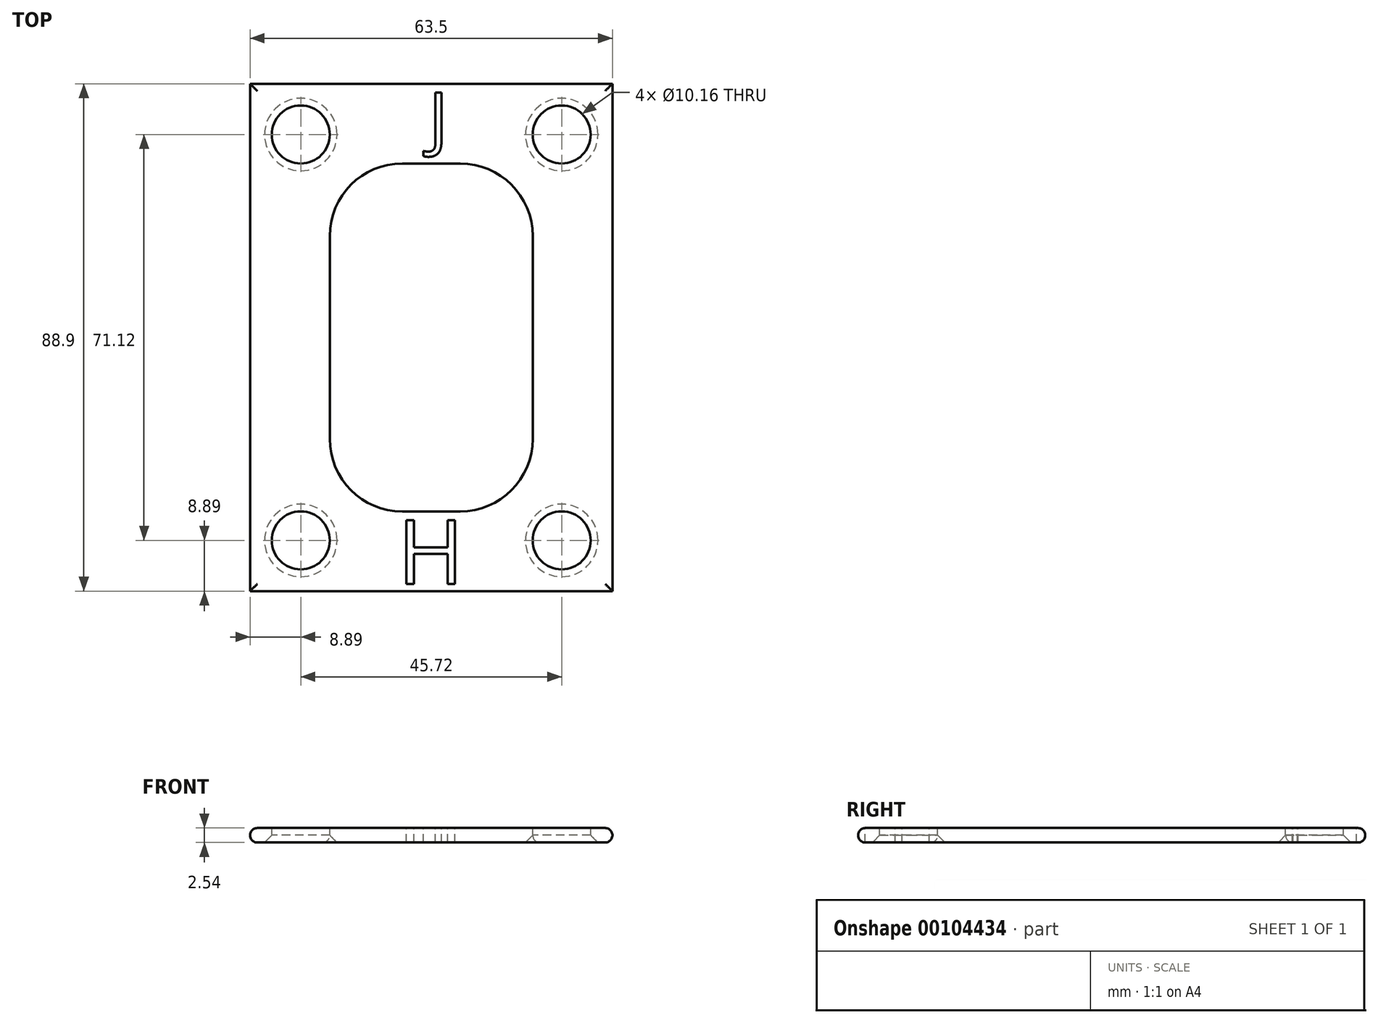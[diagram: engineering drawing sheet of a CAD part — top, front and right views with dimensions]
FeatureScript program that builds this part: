
annotation { "Feature Type Name" : "Feature", "Feature Type Description" : "" }
export const myFeature = defineFeature(function(context is Context, id is Id, definition is map)
    precondition{}
    {
        {
            var Q0;
            Q0=qCreatedBy(makeId("Top.planeOp"),FACE);
            var sketch = newSketch(context, id + "F0", { "sketchPlane" : qUnion([Q0])});
            skPoint(sketch, "E0", {"position": v(0, 88.9) * mm});
            skPoint(sketch, "E1", {"position": v(63.5, 0) * mm});
            skLineSegment(sketch, "E2.bottom", {"start": v(0, 88.9) * mm, "end": v(63.5, 88.9) * mm});
            skLineSegment(sketch, "E2.top", {"start": v(0, 0) * mm, "end": v(63.5, 0) * mm});
            skLineSegment(sketch, "E2.left", {"start": v(0, 88.9) * mm, "end": v(0, 0) * mm});
            skLineSegment(sketch, "E2.right", {"start": v(63.5, 88.9) * mm, "end": v(63.5, 0) * mm});
            skSolve(sketch);
        }
        {
            var Q0;
            Q0 = qSketchRegion(id + "F0", true);
            extrude(context, id + "F1", {"entities" : qUnion([Q0]), "depth" : 2.54 * mm});
        }
        {
            var Q0;
            Q0=makeQuery(id+"F1.opExtrude","CAP_EDGE",EDGE,{"disambiguationData":[OSD([sQuery(id+"F0.wireOp",EDGE,"E2.right")])],"isStart":false});
            var Q1;
            Q1=makeQuery(id+"F1.opExtrude","CAP_EDGE",EDGE,{"disambiguationData":[OSD([sQuery(id+"F0.wireOp",EDGE,"E2.top")])],"isStart":false});
            var Q2;
            Q2=makeQuery(id+"F1.opExtrude","CAP_EDGE",EDGE,{"disambiguationData":[OSD([sQuery(id+"F0.wireOp",EDGE,"E2.bottom")])],"isStart":false});
            var Q3;
            Q3=makeQuery(id+"F1.opExtrude","CAP_EDGE",EDGE,{"disambiguationData":[OSD([sQuery(id+"F0.wireOp",EDGE,"E2.left")])],"isStart":false});
            var Q4;
            Q4=makeQuery(id+"F1.opExtrude","CAP_FACE",FACE,{"disambiguationData":[OSD([sQuery(id+"F0.wireOp",EDGE,"E2.bottom"),sQuery(id+"F0.wireOp",EDGE,"E2.top"),sQuery(id+"F0.wireOp",EDGE,"E2.left"),sQuery(id+"F0.wireOp",EDGE,"E2.right")])],"isStart":true});
            var Q5;
            Q5=makeQuery(id+"F1.opExtrude","CAP_EDGE",EDGE,{"disambiguationData":[OSD([sQuery(id+"F0.wireOp",EDGE,"E2.left")])],"isStart":true});
            var Q6;
            Q6=makeQuery(id+"F1.opExtrude","CAP_EDGE",EDGE,{"disambiguationData":[OSD([sQuery(id+"F0.wireOp",EDGE,"E2.right")])],"isStart":true});
            var Q7;
            Q7=makeQuery(id+"F1.opExtrude","CAP_EDGE",EDGE,{"disambiguationData":[OSD([sQuery(id+"F0.wireOp",EDGE,"E2.bottom")])],"isStart":true});
            var Q8;
            Q8=makeQuery(id+"F1.opExtrude","CAP_EDGE",EDGE,{"disambiguationData":[OSD([sQuery(id+"F0.wireOp",EDGE,"E2.top")])],"isStart":true});
            fillet(context, id + "F2", {"entities" : qUnion([Q0, Q1, Q2, Q3, Q4, Q5, Q6, Q7, Q8]), "radius" : 1.27 * mm, "tangentPropagation" : true, "allowEdgeOverflow" : false});
        }
        {
            var Q0;
            Q0=makeQuery(id+"F1.opExtrude","CAP_FACE",FACE,{"disambiguationData":[OSD([sQuery(id+"F0.wireOp",EDGE,"E2.bottom"),sQuery(id+"F0.wireOp",EDGE,"E2.top"),sQuery(id+"F0.wireOp",EDGE,"E2.left"),sQuery(id+"F0.wireOp",EDGE,"E2.right")])],"isStart":false});
            var sketch = newSketch(context, id + "F3", { "sketchPlane" : qUnion([Q0])});
            skPoint(sketch, "E3", {"position": v(31.75, 44.45) * mm});
            skPoint(sketch, "E3.positionSnap0", {"position": v(1.27, 44.45) * mm});
            skPoint(sketch, "E3.positionSnap1", {"position": v(31.75, 87.63) * mm});
            skPoint(sketch, "E4", {"position": v(13.97, 74.93) * mm});
            skPoint(sketch, "E5", {"position": v(49.53, 74.93) * mm});
            skPoint(sketch, "E6", {"position": v(49.53, 13.97) * mm});
            skLineSegment(sketch, "E7.bottom", {"start": v(26.67, 74.93) * mm, "end": v(36.83, 74.93) * mm});
            skLineSegment(sketch, "E7.top", {"start": v(26.67, 13.97) * mm, "end": v(36.83, 13.97) * mm});
            skLineSegment(sketch, "E7.left", {"start": v(13.97, 62.23) * mm, "end": v(13.97, 26.67) * mm});
            skLineSegment(sketch, "E7.right", {"start": v(49.53, 62.23) * mm, "end": v(49.53, 26.67) * mm});
            skArc(sketch, "E8.filletArc", {"start": v(49.53, 62.23) * mm, "mid": v(45.81, 71.21) * mm, "end": v(36.83, 74.93) * mm});
            skArc(sketch, "E9.filletArc", {"start": v(26.67, 74.93) * mm, "mid": v(17.69, 71.21) * mm, "end": v(13.97, 62.23) * mm});
            skPoint(sketch, "E10.visualSharp", {"position": v(13.97, 13.97) * mm});
            skArc(sketch, "E10.filletArc", {"start": v(13.97, 26.67) * mm, "mid": v(17.69, 17.69) * mm, "end": v(26.67, 13.97) * mm});
            skArc(sketch, "E11.filletArc", {"start": v(36.83, 13.97) * mm, "mid": v(45.81, 17.69) * mm, "end": v(49.53, 26.67) * mm});
            skSolve(sketch);
        }
        {
            var Q0;
            Q0 = qSketchRegion(id + "F3", true);
            extrude(context, id + "F4", {"entities" : qUnion([Q0]), "operationType" : NewBodyOperationType.REMOVE, "endBound" : BoundingType.THROUGH_ALL, "oppositeDirection" : true, "depth" : 25.4 * mm});
        }
        {
            var Q0;
            Q0=makeQuery(id+"F4.boolean.opBoolean","COPY",EDGE,{"derivedFrom":makeQuery(id+"F4.opExtrude","CAP_EDGE",EDGE,{"disambiguationData":[OSD([sQuery(id+"F3.wireOp",EDGE,"E8.filletArc")])],"isStart":true})});
            var Q1;
            Q1=makeQuery(id+"F4.boolean.opBoolean","INTERSECT",EDGE,{"derivedFrom":[makeQuery(id+"F1.opExtrude","CAP_FACE",FACE,{"disambiguationData":[OSD([sQuery(id+"F0.wireOp",EDGE,"E2.bottom"),sQuery(id+"F0.wireOp",EDGE,"E2.top"),sQuery(id+"F0.wireOp",EDGE,"E2.left"),sQuery(id+"F0.wireOp",EDGE,"E2.right")])],"isStart":true}),makeQuery(id+"F4.opExtrude","SWEPT_FACE",FACE,{"disambiguationData":[OSD([sQuery(id+"F3.wireOp",EDGE,"E7.left")])]})]});
            fillet(context, id + "F5", {"entities" : qUnion([Q0, Q1]), "radius" : 1.27 * mm, "tangentPropagation" : true, "allowEdgeOverflow" : false});
        }
        {
            var Q0;
            Q0=makeQuery(id+"F1.opExtrude","CAP_FACE",FACE,{"disambiguationData":[OSD([sQuery(id+"F0.wireOp",EDGE,"E2.bottom"),sQuery(id+"F0.wireOp",EDGE,"E2.top"),sQuery(id+"F0.wireOp",EDGE,"E2.left"),sQuery(id+"F0.wireOp",EDGE,"E2.right")])],"isStart":false});
            var sketch = newSketch(context, id + "F6", { "sketchPlane" : qUnion([Q0])});
            skPoint(sketch, "E12", {"position": v(8.9, 80.01) * mm});
            skPoint(sketch, "E13", {"position": v(54.6, 80.01) * mm});
            skPoint(sketch, "E14", {"position": v(54.6, 8.9) * mm});
            skPoint(sketch, "E15", {"position": v(8.9, 8.9) * mm});
            skPoint(sketch, "E16", {"position": v(13.97, 80.01) * mm});
            skPoint(sketch, "E17", {"position": v(13.97, 8.9) * mm});
            skPoint(sketch, "E18", {"position": v(49.53, 80.01) * mm});
            skPoint(sketch, "E19", {"position": v(49.53, 8.9) * mm});
            skCircle(sketch, "E20", {"center": v(8.9, 80.01) * mm, "radius": 5.08 * mm});
            skCircle(sketch, "E21", {"center": v(54.6, 80.01) * mm, "radius": 5.08 * mm});
            skCircle(sketch, "E22", {"center": v(54.6, 8.9) * mm, "radius": 5.08 * mm});
            skCircle(sketch, "E23", {"center": v(8.9, 8.9) * mm, "radius": 5.08 * mm});
            skSolve(sketch);
        }
        {
            var Q0;
            Q0 = qSketchRegion(id + "F6", true);
            extrude(context, id + "F7", {"entities" : qUnion([Q0]), "operationType" : NewBodyOperationType.REMOVE, "endBound" : BoundingType.THROUGH_ALL, "oppositeDirection" : true, "depth" : 25.4 * mm});
        }
        {
            var Q0;
            Q0=makeQuery(id+"F7.boolean.opBoolean","INTERSECT",EDGE,{"derivedFrom":[makeQuery(id+"F1.opExtrude","CAP_FACE",FACE,{"disambiguationData":[OSD([sQuery(id+"F0.wireOp",EDGE,"E2.bottom"),sQuery(id+"F0.wireOp",EDGE,"E2.top"),sQuery(id+"F0.wireOp",EDGE,"E2.left"),sQuery(id+"F0.wireOp",EDGE,"E2.right")])],"isStart":true}),makeQuery(id+"F7.opExtrude","SWEPT_FACE",FACE,{"disambiguationData":[OSD([sQuery(id+"F6.wireOp",EDGE,"E20")])]})]});
            var Q1;
            Q1=makeQuery(id+"F7.boolean.opBoolean","COPY",EDGE,{"derivedFrom":makeQuery(id+"F7.opExtrude","CAP_EDGE",EDGE,{"disambiguationData":[OSD([sQuery(id+"F6.wireOp",EDGE,"E20")])],"isStart":true})});
            var Q2;
            Q2=makeQuery(id+"F7.boolean.opBoolean","COPY",EDGE,{"derivedFrom":makeQuery(id+"F7.opExtrude","CAP_EDGE",EDGE,{"disambiguationData":[OSD([sQuery(id+"F6.wireOp",EDGE,"E21")])],"isStart":true})});
            var Q3;
            Q3=makeQuery(id+"F7.boolean.opBoolean","INTERSECT",EDGE,{"derivedFrom":[makeQuery(id+"F1.opExtrude","CAP_FACE",FACE,{"disambiguationData":[OSD([sQuery(id+"F0.wireOp",EDGE,"E2.bottom"),sQuery(id+"F0.wireOp",EDGE,"E2.top"),sQuery(id+"F0.wireOp",EDGE,"E2.left"),sQuery(id+"F0.wireOp",EDGE,"E2.right")])],"isStart":true}),makeQuery(id+"F7.opExtrude","SWEPT_FACE",FACE,{"disambiguationData":[OSD([sQuery(id+"F6.wireOp",EDGE,"E21")])]})]});
            var Q4;
            Q4=makeQuery(id+"F7.boolean.opBoolean","INTERSECT",EDGE,{"derivedFrom":[makeQuery(id+"F1.opExtrude","CAP_FACE",FACE,{"disambiguationData":[OSD([sQuery(id+"F0.wireOp",EDGE,"E2.bottom"),sQuery(id+"F0.wireOp",EDGE,"E2.top"),sQuery(id+"F0.wireOp",EDGE,"E2.left"),sQuery(id+"F0.wireOp",EDGE,"E2.right")])],"isStart":true}),makeQuery(id+"F7.opExtrude","SWEPT_FACE",FACE,{"disambiguationData":[OSD([sQuery(id+"F6.wireOp",EDGE,"E22")])]})]});
            var Q5;
            Q5=makeQuery(id+"F7.boolean.opBoolean","COPY",EDGE,{"derivedFrom":makeQuery(id+"F7.opExtrude","CAP_EDGE",EDGE,{"disambiguationData":[OSD([sQuery(id+"F6.wireOp",EDGE,"E22")])],"isStart":true})});
            var Q6;
            Q6=makeQuery(id+"F7.boolean.opBoolean","INTERSECT",EDGE,{"derivedFrom":[makeQuery(id+"F1.opExtrude","CAP_FACE",FACE,{"disambiguationData":[OSD([sQuery(id+"F0.wireOp",EDGE,"E2.bottom"),sQuery(id+"F0.wireOp",EDGE,"E2.top"),sQuery(id+"F0.wireOp",EDGE,"E2.left"),sQuery(id+"F0.wireOp",EDGE,"E2.right")])],"isStart":true}),makeQuery(id+"F7.opExtrude","SWEPT_FACE",FACE,{"disambiguationData":[OSD([sQuery(id+"F6.wireOp",EDGE,"E23")])]})]});
            var Q7;
            Q7=makeQuery(id+"F7.boolean.opBoolean","COPY",EDGE,{"derivedFrom":makeQuery(id+"F7.opExtrude","CAP_EDGE",EDGE,{"disambiguationData":[OSD([sQuery(id+"F6.wireOp",EDGE,"E23")])],"isStart":true})});
            chamfer(context, id + "F8", {"entities" : qUnion([Q0, Q1, Q2, Q3, Q4, Q5, Q6, Q7]), "width" : 1.27 * mm, "tangentPropagation" : true});
        }
        {
            var Q0;
            Q0=makeQuery(id+"F1.opExtrude","CAP_FACE",FACE,{"disambiguationData":[OSD([sQuery(id+"F0.wireOp",EDGE,"E2.bottom"),sQuery(id+"F0.wireOp",EDGE,"E2.top"),sQuery(id+"F0.wireOp",EDGE,"E2.left"),sQuery(id+"F0.wireOp",EDGE,"E2.right")])],"isStart":false});
            var sketch = newSketch(context, id + "F9", { "sketchPlane" : qUnion([Q0])});
            skText(sketch, "E24", { "text": "J", "fontName": "OpenSans-Regular.ttf"});
            skText(sketch, "E25", { "text": "H", "fontName": "OpenSans-Regular.ttf"});
            const initialGuessF9  = {"E24": [0.03133, 0.07844, 1, 0, 0.009], "E25": [0.02587, 0.00127, 1, 0, 0.01128]};
            skSetInitialGuess(sketch, initialGuessF9);
            skSolve(sketch);
        }
        {
            var Q0;
            Q0 = qSketchRegion(id + "F9", true);
            extrude(context, id + "F10", {"entities" : qUnion([Q0]), "operationType" : NewBodyOperationType.REMOVE, "oppositeDirection" : true, "depth" : 25.4 * mm});
        }
    });
